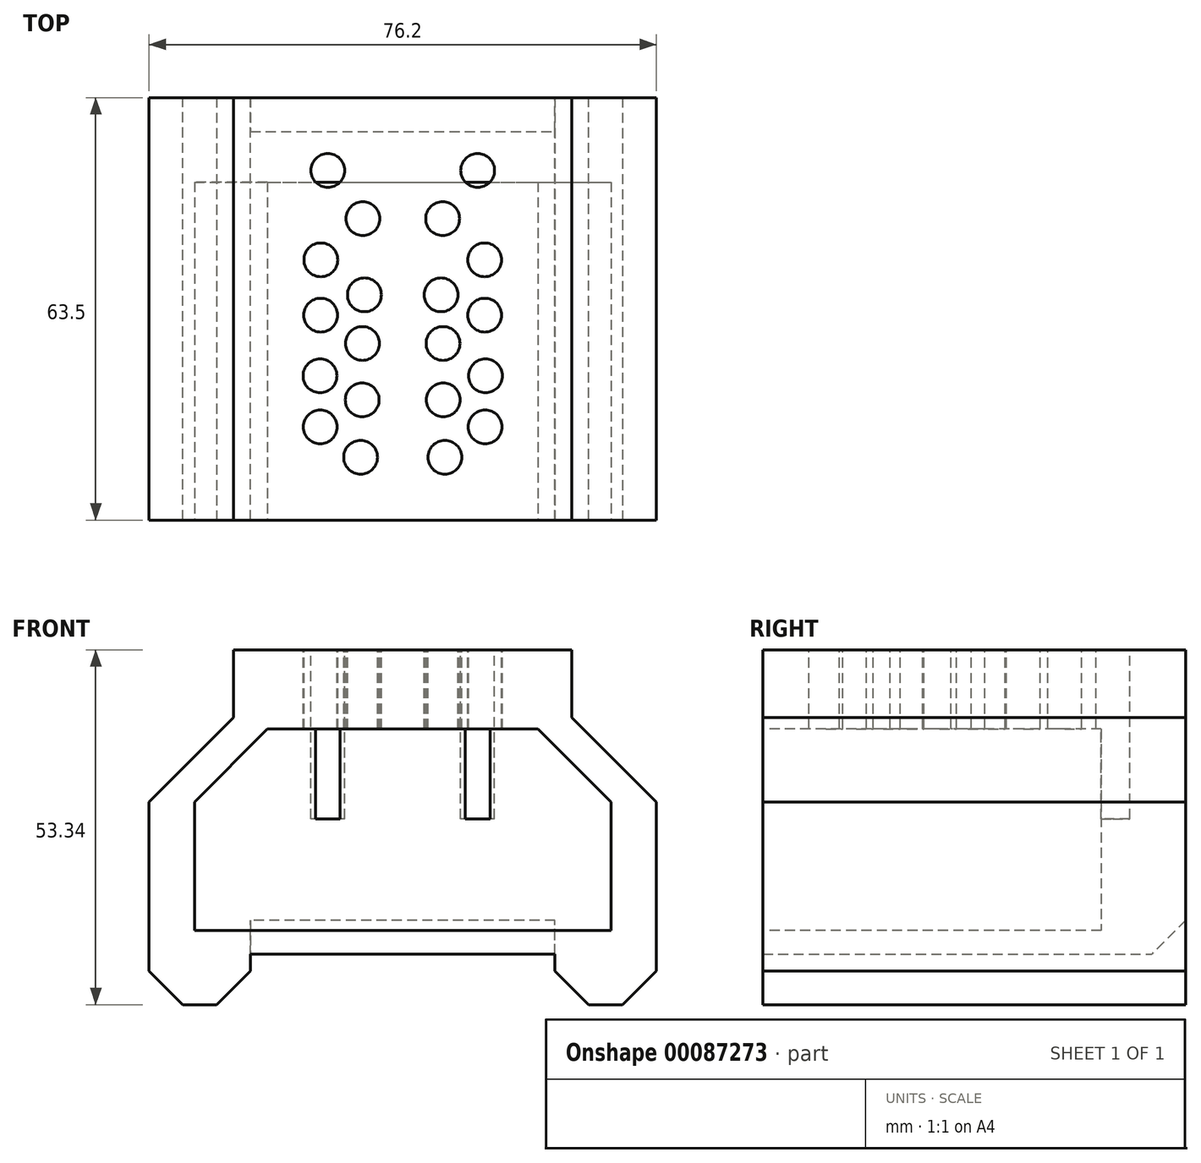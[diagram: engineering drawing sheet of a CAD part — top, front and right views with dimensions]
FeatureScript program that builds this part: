
annotation { "Feature Type Name" : "Feature", "Feature Type Description" : "" }
export const myFeature = defineFeature(function(context is Context, id is Id, definition is map)
    precondition{}
    {
        {
            var Q0;
            Q0=qCreatedBy(makeId("Front.planeOp"),FACE);
            var sketch = newSketch(context, id + "F0", { "sketchPlane" : qUnion([Q0])});
            skLineSegment(sketch, "E0.bottom", {"start": v(25.4, 25.4) * mm, "end": v(-25.4, 25.4) * mm});
            skLineSegment(sketch, "E0.top", {"start": v(25.4, -25.4) * mm, "end": v(-25.4, -25.4) * mm});
            skLineSegment(sketch, "E0.left", {"start": v(25.4, 25.4) * mm, "end": v(25.4, -25.4) * mm});
            skLineSegment(sketch, "E0.right", {"start": v(-25.4, 25.4) * mm, "end": v(-25.4, -25.4) * mm});
            skPoint(sketch, "E0.middle", {"position": v(0, 0) * mm});
            skSolve(sketch);
        }
        {
            var Q0;
            Q0 = qSketchRegion(id + "F0", true);
            extrude(context, id + "F1", {"entities" : qUnion([Q0]), "depth" : 63.5 * mm});
        }
        {
            var Q0;
            Q0=makeQuery(id+"F1.opExtrude","SWEPT_FACE",FACE,{"disambiguationData":[OSD([sQuery(id+"F0.wireOp",EDGE,"E0.left")])]});
            var sketch = newSketch(context, id + "F2", { "sketchPlane" : qUnion([Q0])});
            skLineSegment(sketch, "E1", {"start": v(-63.5, 0) * mm, "end": v(0, 0) * mm});
            skSolve(sketch);
        }
        {
            var Q0;
            Q0 = qSketchRegion(id + "F2", true);
            var Q1;
            {var subQ0=sQuery(id+"F2.wireOp",EDGE,"E1");Q1=makeQuery(id+"F2.imprint","IMPRINT",FACE,{"disambiguationData":[TD([[makeQuery(id+"F2.imprint","IMPRINT",EDGE,{"derivedFrom":subQ0}),-1.0]])]});}
            extrude(context, id + "F3", {"entities" : qUnion([Q0, Q1]), "operationType" : NewBodyOperationType.ADD, "depth" : 12.7 * mm});
        }
        {
            var Q0;
            Q0=makeQuery(id+"F3.opExtrude","SWEPT_FACE",FACE,{"disambiguationData":[OSD([sQuery(id+"F2.wireOp",EDGE,"E1")])]});
            extrude(context, id + "F4", {"entities" : qUnion([Q0]), "operationType" : NewBodyOperationType.ADD, "depth" : 10.16 * mm});
        }
        {
            var Q0;
            Q0=makeQuery(id+"F1.opExtrude","SWEPT_FACE",FACE,{"disambiguationData":[OSD([sQuery(id+"F0.wireOp",EDGE,"E0.right")])]});
            var sketch = newSketch(context, id + "F5", { "sketchPlane" : qUnion([Q0])});
            skLineSegment(sketch, "E2", {"start": v(0, 0) * mm, "end": v(63.5, 0) * mm});
            skSolve(sketch);
        }
        {
            var Q0;
            Q0 = qSketchRegion(id + "F5", true);
            var Q1;
            {var subQ0=sQuery(id+"F5.wireOp",EDGE,"E2");Q1=makeQuery(id+"F5.imprint","IMPRINT",FACE,{"disambiguationData":[TD([[makeQuery(id+"F5.imprint","IMPRINT",EDGE,{"derivedFrom":subQ0}),-1.0]])]});}
            extrude(context, id + "F6", {"entities" : qUnion([Q0, Q1]), "operationType" : NewBodyOperationType.ADD, "depth" : 12.7 * mm});
        }
        {
            var Q0;
            Q0=makeQuery(id+"F6.opExtrude","SWEPT_FACE",FACE,{"disambiguationData":[OSD([sQuery(id+"F5.wireOp",EDGE,"E2")])]});
            extrude(context, id + "F7", {"entities" : qUnion([Q0]), "operationType" : NewBodyOperationType.ADD, "depth" : 10.16 * mm});
        }
        {
            var Q0;
            {var subQ0=sQuery(id+"F5.wireOp",EDGE,"E2");Q0=makeQuery(id+"F7.opExtrude","CAP_EDGE",EDGE,{"disambiguationData":[OSD([subQ0]),TDD([makeQuery(id+"F6.opExtrude","CAP_EDGE",EDGE,{"disambiguationData":[OSD([subQ0])],"isStart":false})])],"isStart":false});}
            var Q1;
            {var subQ0=sQuery(id+"F2.wireOp",EDGE,"E1");Q1=makeQuery(id+"F4.opExtrude","CAP_EDGE",EDGE,{"disambiguationData":[OSD([subQ0]),TDD([makeQuery(id+"F3.opExtrude","CAP_EDGE",EDGE,{"disambiguationData":[OSD([subQ0])],"isStart":false})])],"isStart":false});}
            chamfer(context, id + "F8", {"entities" : qUnion([Q0, Q1]), "width" : 12.7 * mm, "tangentPropagation" : true});
        }
        {
            var Q0;
            Q0=makeQuery(id+"F1.opExtrude","SWEPT_FACE",FACE,{"disambiguationData":[OSD([sQuery(id+"F0.wireOp",EDGE,"E0.bottom")])]});
            extrude(context, id + "F9", {"entities" : qUnion([Q0]), "operationType" : NewBodyOperationType.REMOVE, "oppositeDirection" : true, "depth" : 5.08 * mm});
        }
        {
            var Q0;
            {var subQ0=sQuery(id+"F0.wireOp",EDGE,"E0.top");Q0=makeQuery(id+"F6.boolean.opBoolean","MERGE",FACE,{"derivedFrom":[makeQuery(id+"F3.boolean.opBoolean","MERGE",FACE,{"derivedFrom":[makeQuery(id+"F1.opExtrude","SWEPT_FACE",FACE,{"disambiguationData":[OSD([subQ0])]}),makeQuery(id+"F3.opExtrude","SWEPT_FACE",FACE,{"disambiguationData":[OSD([subQ0,sQuery(id+"F0.wireOp",EDGE,"E0.left")])]})]}),makeQuery(id+"F6.opExtrude","SWEPT_FACE",FACE,{"disambiguationData":[OSD([subQ0,sQuery(id+"F0.wireOp",EDGE,"E0.right")])]})]});}
            var sketch = newSketch(context, id + "F10", { "sketchPlane" : qUnion([Q0])});
            skLineSegment(sketch, "E3", {"start": v(-22.86, 63.5) * mm, "end": v(-22.86, 0) * mm});
            skLineSegment(sketch, "E4", {"start": v(22.86, 63.5) * mm, "end": v(22.86, 0) * mm});
            skSolve(sketch);
        }
        {
            var Q0;
            Q0 = qSketchRegion(id + "F10", true);
            var Q1;
            {var subQ0=sQuery(id+"F10.wireOp",EDGE,"E3");Q1=makeQuery(id+"F10.imprint","IMPRINT",FACE,{"disambiguationData":[TD([[makeQuery(id+"F10.imprint","IMPRINT",EDGE,{"derivedFrom":subQ0}),-1.0]])]});}
            var Q2;
            {var subQ0=sQuery(id+"F10.wireOp",EDGE,"E4");Q2=makeQuery(id+"F10.imprint","IMPRINT",FACE,{"disambiguationData":[TD([[makeQuery(id+"F10.imprint","IMPRINT",EDGE,{"derivedFrom":subQ0}),1.0]])]});}
            extrude(context, id + "F11", {"entities" : qUnion([Q0, Q1, Q2]), "operationType" : NewBodyOperationType.ADD, "depth" : 7.62 * mm});
        }
        {
            var Q0;
            Q0=makeQuery(id+"F11.opExtrude","CAP_EDGE",EDGE,{"disambiguationData":[OSD([sQuery(id+"F10.wireOp",EDGE,"E3")])],"isStart":false});
            var Q1;
            Q1=makeQuery(id+"F11.opExtrude","CAP_EDGE",EDGE,{"disambiguationData":[OSD([sQuery(id+"F0.wireOp",EDGE,"E0.top"),sQuery(id+"F0.wireOp",EDGE,"E0.right")])],"isStart":false});
            var Q2;
            Q2=makeQuery(id+"F11.opExtrude","CAP_EDGE",EDGE,{"disambiguationData":[OSD([sQuery(id+"F10.wireOp",EDGE,"E4")])],"isStart":false});
            var Q3;
            Q3=makeQuery(id+"F11.opExtrude","CAP_EDGE",EDGE,{"disambiguationData":[OSD([sQuery(id+"F0.wireOp",EDGE,"E0.top"),sQuery(id+"F0.wireOp",EDGE,"E0.left")])],"isStart":false});
            var Q4;
            {var subQ0=sQuery(id+"F0.wireOp",EDGE,"E0.right");var subQ1=sQuery(id+"F0.wireOp",EDGE,"E0.top");var subQ2=sQuery(id+"F0.wireOp",EDGE,"E0.left");Q4=makeQuery(id+"F6.boolean.opBoolean","MERGE",EDGE,{"derivedFrom":[makeQuery(id+"F3.boolean.opBoolean","MERGE",EDGE,{"derivedFrom":[makeQuery(id+"F1.opExtrude","CAP_EDGE",EDGE,{"disambiguationData":[OSD([subQ1])],"isStart":true}),makeQuery(id+"F3.opExtrude","SWEPT_EDGE",EDGE,{"disambiguationData":[OSD([subQ1,subQ2]),TDD([makeQuery(id+"F2.imprint","INTERSECT",VERTEX,{"derivedFrom":[makeQuery(id+"F1.opExtrude","SWEPT_EDGE",EDGE,{"disambiguationData":[OSD([subQ1,subQ2])]}),makeQuery(id+"F1.opExtrude","CAP_EDGE",EDGE,{"disambiguationData":[OSD([subQ2])],"isStart":true})]})])]})]}),makeQuery(id+"F6.opExtrude","SWEPT_EDGE",EDGE,{"disambiguationData":[OSD([subQ1,subQ0]),TDD([makeQuery(id+"F5.imprint","INTERSECT",VERTEX,{"derivedFrom":[makeQuery(id+"F1.opExtrude","SWEPT_EDGE",EDGE,{"disambiguationData":[OSD([subQ1,subQ0])]}),makeQuery(id+"F1.opExtrude","CAP_EDGE",EDGE,{"disambiguationData":[OSD([subQ0])],"isStart":true})]})])]})]});}
            var Q5;
            {var subQ0=sQuery(id+"F0.wireOp",EDGE,"E0.bottom");Q5=makeQuery(id+"F9.boolean.opBoolean","COPY",EDGE,{"derivedFrom":makeQuery(id+"F9.opExtrude","CAP_EDGE",EDGE,{"disambiguationData":[OSD([subQ0]),TDD([makeQuery(id+"F1.opExtrude","CAP_EDGE",EDGE,{"disambiguationData":[OSD([subQ0])],"isStart":true})])],"isStart":false})});}
            var Q6;
            Q6=makeQuery(id+"F9.boolean.opBoolean","COPY",EDGE,{"derivedFrom":makeQuery(id+"F9.opExtrude","CAP_EDGE",EDGE,{"disambiguationData":[OSD([sQuery(id+"F0.wireOp",EDGE,"E0.bottom"),sQuery(id+"F0.wireOp",EDGE,"E0.left")])],"isStart":false})});
            var Q7;
            Q7=makeQuery(id+"F9.boolean.opBoolean","COPY",EDGE,{"derivedFrom":makeQuery(id+"F9.opExtrude","CAP_EDGE",EDGE,{"disambiguationData":[OSD([sQuery(id+"F0.wireOp",EDGE,"E0.bottom"),sQuery(id+"F0.wireOp",EDGE,"E0.right")])],"isStart":false})});
            chamfer(context, id + "F12", {"entities" : qUnion([Q0, Q1, Q2, Q3, Q4, Q5, Q6, Q7]), "width" : 5.08 * mm, "tangentPropagation" : true});
        }
        {
            var Q0;
            Q0=makeQuery(id+"F9.boolean.opBoolean","COPY",FACE,{"derivedFrom":makeQuery(id+"F9.opExtrude","CAP_FACE",FACE,{"disambiguationData":[OSD([sQuery(id+"F0.wireOp",EDGE,"E0.bottom")])],"isStart":false})});
            var sketch = newSketch(context, id + "F13", { "sketchPlane" : qUnion([Q0])});
            skCircle(sketch, "E5", {"center": v(-11.25, -10.96) * mm, "radius": 2.54 * mm});
            skCircle(sketch, "E6", {"center": v(-6, -18.2) * mm, "radius": 2.54 * mm});
            skCircle(sketch, "E7", {"center": v(-12.3, -24.39) * mm, "radius": 2.54 * mm});
            skCircle(sketch, "E8", {"center": v(-5.75, -29.65) * mm, "radius": 2.54 * mm});
            skCircle(sketch, "E9", {"center": v(-12.32, -32.7) * mm, "radius": 2.54 * mm});
            skCircle(sketch, "E10", {"center": v(-6.05, -36.96) * mm, "radius": 2.54 * mm});
            skCircle(sketch, "E11", {"center": v(-12.42, -41.83) * mm, "radius": 2.54 * mm});
            skCircle(sketch, "E12", {"center": v(-6.1, -45.44) * mm, "radius": 2.54 * mm});
            skCircle(sketch, "E13", {"center": v(-12.39, -49.5) * mm, "radius": 2.54 * mm});
            skCircle(sketch, "E14", {"center": v(-6.33, -54.06) * mm, "radius": 2.54 * mm});
            skLineSegment(sketch, "E15", {"start": v(0, 9.18) * mm, "end": v(0, -69.78) * mm, "construction": true});
            skCircle(sketch, "E16.MirrorC", {"center": v(11.25, -10.96) * mm, "radius": 2.54 * mm});
            skCircle(sketch, "E17.MirrorC", {"center": v(6, -18.2) * mm, "radius": 2.54 * mm});
            skCircle(sketch, "E18.MirrorC", {"center": v(12.3, -24.39) * mm, "radius": 2.54 * mm});
            skCircle(sketch, "E19.MirrorC", {"center": v(5.75, -29.65) * mm, "radius": 2.54 * mm});
            skCircle(sketch, "E20.MirrorC", {"center": v(12.32, -32.7) * mm, "radius": 2.54 * mm});
            skCircle(sketch, "E21.MirrorC", {"center": v(6.05, -36.96) * mm, "radius": 2.54 * mm});
            skCircle(sketch, "E22.MirrorC", {"center": v(12.42, -41.83) * mm, "radius": 2.54 * mm});
            skCircle(sketch, "E23.MirrorC", {"center": v(6.1, -45.44) * mm, "radius": 2.54 * mm});
            skCircle(sketch, "E24.MirrorC", {"center": v(12.39, -49.5) * mm, "radius": 2.54 * mm});
            skCircle(sketch, "E25.MirrorC", {"center": v(6.33, -54.06) * mm, "radius": 2.54 * mm});
            skSolve(sketch);
        }
        {
            var Q0;
            Q0 = qSketchRegion(id + "F13", true);
            extrude(context, id + "F14", {"entities" : qUnion([Q0]), "operationType" : NewBodyOperationType.REMOVE, "oppositeDirection" : true, "depth" : 25.4 * mm});
        }
        {
            var Q0;
            Q0=makeQuery(id+"F8.opChamfer","BLEND_FACE",FACE,{"disambiguationData":[OSD([sQuery(id+"F2.wireOp",EDGE,"E1")])]});
            var sketch = newSketch(context, id + "F15", { "sketchPlane" : qUnion([Q0])});
            skLineSegment(sketch, "E26.bottom", {"start": v(13.96, -3.31) * mm, "end": v(26.66, -3.31) * mm});
            skLineSegment(sketch, "E26.top", {"start": v(13.96, -61.45) * mm, "end": v(26.66, -61.45) * mm});
            skLineSegment(sketch, "E26.left", {"start": v(13.96, -3.31) * mm, "end": v(13.96, -61.45) * mm});
            skLineSegment(sketch, "E26.right", {"start": v(26.66, -3.31) * mm, "end": v(26.66, -61.45) * mm});
            skSolve(sketch);
        }
        {
            var Q0;
            Q0 = qSketchRegion(id + "F15", true);
            extrude(context, id + "F16", {"entities" : qUnion([Q0]), "operationType" : NewBodyOperationType.REMOVE, "oppositeDirection" : true, "depth" : 12.7 * mm});
        }
        {
            var Q0;
            Q0=makeQuery(id+"F8.opChamfer","BLEND_FACE",FACE,{"disambiguationData":[OSD([sQuery(id+"F5.wireOp",EDGE,"E2")])]});
            var sketch = newSketch(context, id + "F17", { "sketchPlane" : qUnion([Q0])});
            skLineSegment(sketch, "E27.bottom", {"start": v(-13.43, -2.93) * mm, "end": v(-26.13, -2.93) * mm});
            skLineSegment(sketch, "E27.top", {"start": v(-13.43, -61.07) * mm, "end": v(-26.13, -61.07) * mm});
            skLineSegment(sketch, "E27.left", {"start": v(-13.43, -2.93) * mm, "end": v(-13.43, -61.07) * mm});
            skLineSegment(sketch, "E27.right", {"start": v(-26.13, -2.93) * mm, "end": v(-26.13, -61.07) * mm});
            skSolve(sketch);
        }
        {
            var Q0;
            Q0=makeQuery(id+"F17.imprint","IMPRINT",FACE,{"disambiguationData":[TD([[makeQuery(id+"F17.imprint","IMPRINT",EDGE,{"derivedFrom":sQuery(id+"F17.wireOp",EDGE,"E27.bottom")}),1.0]])]});
            extrude(context, id + "F18", {"entities" : qUnion([Q0]), "operationType" : NewBodyOperationType.REMOVE, "oppositeDirection" : true, "depth" : 12.7 * mm});
        }
        {
            var Q0;
            {var subQ0=sQuery(id+"F0.wireOp",EDGE,"E0.right");var subQ1=makeQuery(id+"F1.opExtrude","CAP_EDGE",EDGE,{"disambiguationData":[OSD([subQ0])],"isStart":false});var subQ2=sQuery(id+"F0.wireOp",EDGE,"E0.top");var subQ3=makeQuery(id+"F5.imprint","INTERSECT",VERTEX,{"derivedFrom":[makeQuery(id+"F1.opExtrude","SWEPT_EDGE",EDGE,{"disambiguationData":[OSD([subQ2,subQ0])]}),subQ1]});var subQ4=sQuery(id+"F0.wireOp",EDGE,"E0.left");var subQ5=makeQuery(id+"F1.opExtrude","CAP_EDGE",EDGE,{"disambiguationData":[OSD([subQ4])],"isStart":false});var subQ6=makeQuery(id+"F2.imprint","INTERSECT",VERTEX,{"derivedFrom":[makeQuery(id+"F1.opExtrude","SWEPT_EDGE",EDGE,{"disambiguationData":[OSD([subQ2,subQ4])]}),subQ5]});var subQ7=makeQuery(id+"F6.boolean.opBoolean","MERGE",EDGE,{"derivedFrom":[makeQuery(id+"F3.boolean.opBoolean","MERGE",EDGE,{"derivedFrom":[makeQuery(id+"F1.opExtrude","CAP_EDGE",EDGE,{"disambiguationData":[OSD([subQ2])],"isStart":false}),makeQuery(id+"F3.opExtrude","SWEPT_EDGE",EDGE,{"disambiguationData":[OSD([subQ2,subQ4]),TDD([subQ6])]})]}),makeQuery(id+"F6.opExtrude","SWEPT_EDGE",EDGE,{"disambiguationData":[OSD([subQ2,subQ0]),TDD([subQ3])]})]});var subQ8=sQuery(id+"F5.wireOp",EDGE,"E2");var subQ9=makeQuery(id+"F5.imprint","INTERSECT",VERTEX,{"derivedFrom":[subQ1,subQ8]});var subQ10=sQuery(id+"F2.wireOp",EDGE,"E1");var subQ11=makeQuery(id+"F2.imprint","INTERSECT",VERTEX,{"derivedFrom":[subQ5,subQ10]});Q0=makeQuery(id+"F11.boolean.opBoolean","MERGE",FACE,{"derivedFrom":[makeQuery(id+"F7.boolean.opBoolean","MERGE",FACE,{"derivedFrom":[makeQuery(id+"F6.boolean.opBoolean","MERGE",FACE,{"derivedFrom":[makeQuery(id+"F4.boolean.opBoolean","MERGE",FACE,{"derivedFrom":[makeQuery(id+"F3.boolean.opBoolean","MERGE",FACE,{"derivedFrom":[makeQuery(id+"F1.opExtrude","CAP_FACE",FACE,{"disambiguationData":[OSD([sQuery(id+"F0.wireOp",EDGE,"E0.bottom"),subQ2,subQ4,subQ0])],"isStart":false}),makeQuery(id+"F3.opExtrude","SWEPT_FACE",FACE,{"disambiguationData":[OSD([subQ4]),TDD([makeQuery(id+"F2.imprint","IMPRINT",EDGE,{"disambiguationData":[TD([[subQ11,-1.0]])],"derivedFrom":subQ5})])]})]}),makeQuery(id+"F4.opExtrude","SWEPT_FACE",FACE,{"disambiguationData":[OSD([subQ4,subQ10]),TDD([makeQuery(id+"F3.opExtrude","SWEPT_EDGE",EDGE,{"disambiguationData":[OSD([subQ4,subQ10]),TDD([subQ11])]})])]})]}),makeQuery(id+"F6.opExtrude","SWEPT_FACE",FACE,{"disambiguationData":[OSD([subQ0]),TDD([makeQuery(id+"F5.imprint","IMPRINT",EDGE,{"disambiguationData":[TD([[subQ9,-1.0]])],"derivedFrom":subQ1})])]})]}),makeQuery(id+"F7.opExtrude","SWEPT_FACE",FACE,{"disambiguationData":[OSD([subQ0,subQ8]),TDD([makeQuery(id+"F6.opExtrude","SWEPT_EDGE",EDGE,{"disambiguationData":[OSD([subQ0,subQ8]),TDD([subQ9])]})])]})]}),makeQuery(id+"F11.opExtrude","SWEPT_FACE",FACE,{"disambiguationData":[OSD([subQ2,subQ4,subQ0]),TDD([makeQuery(id+"F10.imprint","IMPRINT",EDGE,{"disambiguationData":[TD([[makeQuery(id+"F10.imprint","INTERSECT",VERTEX,{"derivedFrom":[subQ7,sQuery(id+"F10.wireOp",EDGE,"E4")]}),1.0]])],"derivedFrom":subQ7})])]}),makeQuery(id+"F11.opExtrude","SWEPT_FACE",FACE,{"disambiguationData":[OSD([subQ2,subQ4,subQ0]),TDD([makeQuery(id+"F10.imprint","IMPRINT",EDGE,{"disambiguationData":[TD([[makeQuery(id+"F10.imprint","INTERSECT",VERTEX,{"derivedFrom":[subQ7,sQuery(id+"F10.wireOp",EDGE,"E3")]}),-1.0]])],"derivedFrom":subQ7})])]})]});}
            var sketch = newSketch(context, id + "F19", { "sketchPlane" : qUnion([Q0])});
            skLineSegment(sketch, "E28", {"start": v(-20.32, 8.43) * mm, "end": v(20.32, 8.43) * mm});
            skLineSegment(sketch, "E29", {"start": v(20.32, 8.43) * mm, "end": v(31.29, -2.54) * mm});
            skLineSegment(sketch, "E30", {"start": v(31.29, -2.54) * mm, "end": v(31.29, -21.87) * mm});
            skLineSegment(sketch, "E31", {"start": v(31.29, -21.87) * mm, "end": v(0, -21.87) * mm});
            skPoint(sketch, "E32.endSnap0", {"position": v(0, 20.32) * mm});
            skLineSegment(sketch, "E33.MirrorCS", {"start": v(-20.32, 8.43) * mm, "end": v(-31.29, -2.54) * mm});
            skLineSegment(sketch, "E34.MirrorCS", {"start": v(-31.29, -2.54) * mm, "end": v(-31.29, -21.87) * mm});
            skLineSegment(sketch, "E35.MirrorCS", {"start": v(-31.29, -21.87) * mm, "end": v(0, -21.87) * mm});
            skSolve(sketch);
        }
        {
            var Q0;
            Q0 = qSketchRegion(id + "F19", true);
            extrude(context, id + "F20", {"entities" : qUnion([Q0]), "operationType" : NewBodyOperationType.REMOVE, "oppositeDirection" : true, "depth" : 50.8 * mm});
        }
    });
